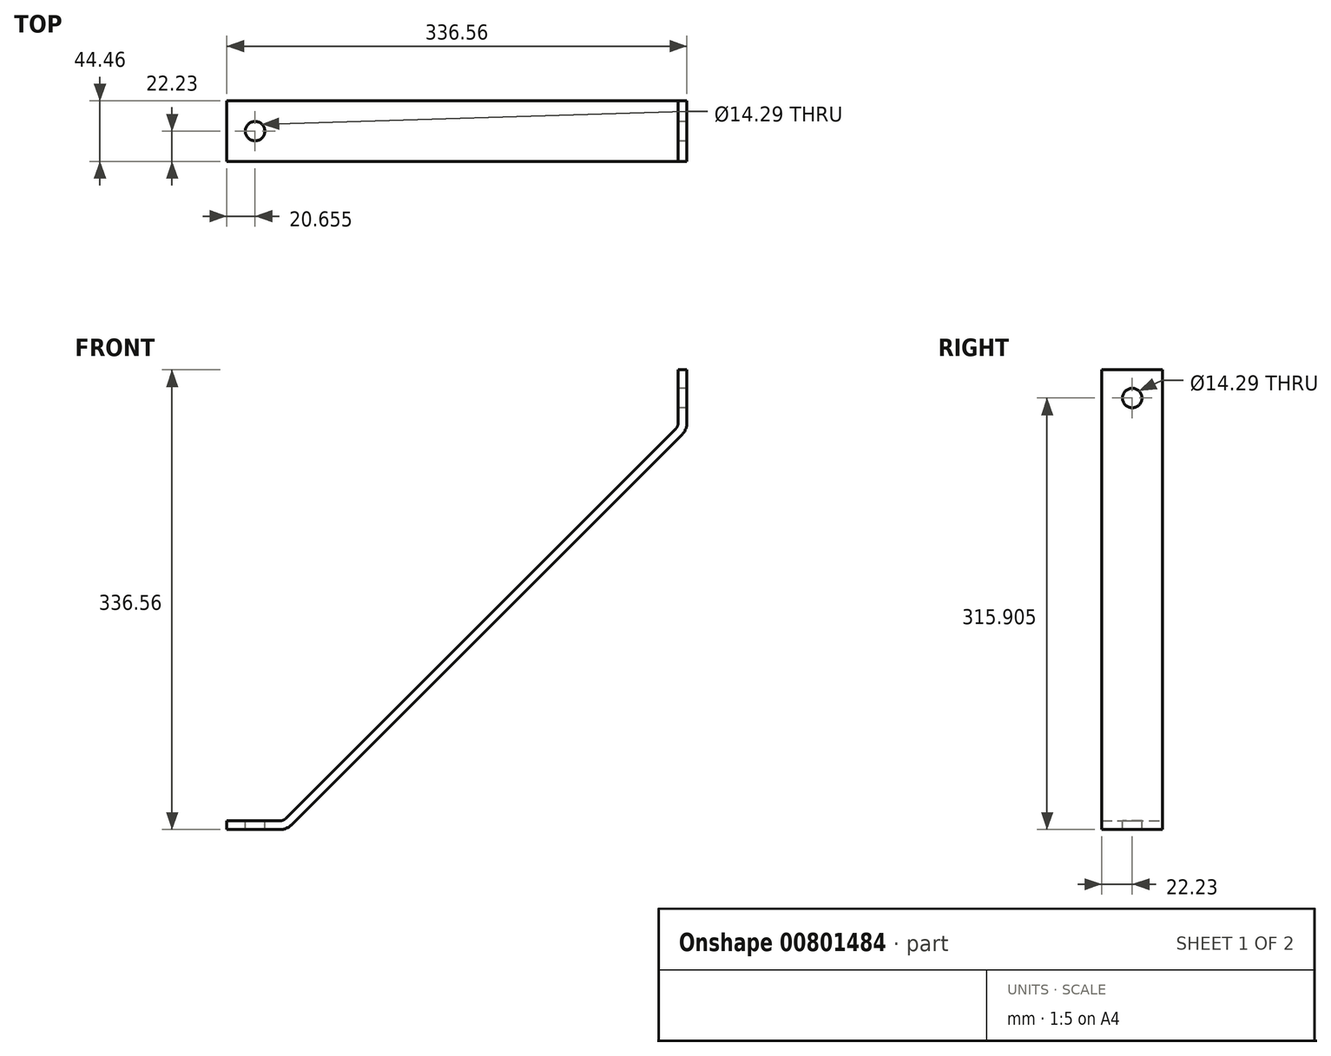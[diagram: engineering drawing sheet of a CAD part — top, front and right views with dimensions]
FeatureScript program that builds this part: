
annotation { "Feature Type Name" : "Feature", "Feature Type Description" : "" }
export const myFeature = defineFeature(function(context is Context, id is Id, definition is map)
    precondition{}
    {
        {
            var Q0;
            Q0=qCreatedBy(makeId("Front.planeOp"),FACE);
            var sketch = newSketch(context, id + "F0", { "sketchPlane" : qUnion([Q0])});
            skLineSegment(sketch, "E0.bottom", {"start": v(-124.37, -168.28) * mm, "end": v(-168.27, -168.28) * mm});
            skLineSegment(sketch, "E0.top", {"start": v(168.27, 168.28) * mm, "end": v(-168.28, 168.27) * mm});
            skLineSegment(sketch, "E0.left", {"start": v(168.27, 124.37) * mm, "end": v(168.27, 168.28) * mm});
            skLineSegment(sketch, "E0.right", {"start": v(-168.27, -168.28) * mm, "end": v(-168.27, -161.93) * mm});
            skPoint(sketch, "E0.middle", {"position": v(0, 0) * mm});
            skLineSegment(sketch, "E1.0", {"start": v(-127, -161.93) * mm, "end": v(-168.27, -161.93) * mm});
            skLineSegment(sketch, "E2", {"start": v(-168.27, -161.93) * mm, "end": v(-127, -161.93) * mm});
            skLineSegment(sketch, "E3", {"start": v(161.92, 168.28) * mm, "end": v(161.92, 127) * mm});
            skLineSegment(sketch, "E4", {"start": v(161.93, 127) * mm, "end": v(-127, -161.93) * mm});
            skLineSegment(sketch, "E5.0", {"start": v(168, 124.1) * mm, "end": v(-124.1, -168) * mm});
            skLineSegment(sketch, "E6", {"start": v(168, 124.1) * mm, "end": v(168.27, 124.37) * mm});
            skLineSegment(sketch, "E7", {"start": v(-124.1, -168) * mm, "end": v(-124.37, -168.28) * mm});
            skPoint(sketch, "E8.orphan", {"position": v(168.28, -168.27) * mm});
            skSolve(sketch);
        }
        {
            var Q0;
            Q0 = qSketchRegion(id + "F0", true);
            extrude(context, id + "F1", {"entities" : qUnion([Q0]), "endBound" : BoundingType.SYMMETRIC, "depth" : 44.45 * mm, "offsetDistance" : 25.4 * mm});
        }
        {
            var Q0;
            Q0=makeQuery(id+"F1.opExtrude","SWEPT_EDGE",EDGE,{"disambiguationData":[OSD([sQuery(id+"F0.wireOp",EDGE,"E2"),sQuery(id+"F0.wireOp",EDGE,"E4")])]});
            var Q1;
            Q1=makeQuery(id+"F1.opExtrude","SWEPT_EDGE",EDGE,{"disambiguationData":[OSD([sQuery(id+"F0.wireOp",EDGE,"E3"),sQuery(id+"F0.wireOp",EDGE,"E4")])]});
            fillet(context, id + "F2", {"entities" : qUnion([Q0, Q1]), "radius" : 6.35 * mm, "tangentPropagation" : true, "allowEdgeOverflow" : false});
        }
        {
            var Q0;
            Q0=makeQuery(id+"F1.opExtrude","SWEPT_EDGE",EDGE,{"disambiguationData":[OSD([sQuery(id+"F0.wireOp",EDGE,"E0.bottom"),sQuery(id+"F0.wireOp",EDGE,"E7")])]});
            var Q1;
            Q1=makeQuery(id+"F1.opExtrude","SWEPT_EDGE",EDGE,{"disambiguationData":[OSD([sQuery(id+"F0.wireOp",EDGE,"E0.left"),sQuery(id+"F0.wireOp",EDGE,"E6")])]});
            fillet(context, id + "F3", {"entities" : qUnion([Q0, Q1]), "radius" : 12.7 * mm, "tangentPropagation" : true, "allowEdgeOverflow" : false});
        }
        {
            var Q0;
            Q0=makeQuery(id+"F1.opExtrude","SWEPT_FACE",FACE,{"disambiguationData":[OSD([sQuery(id+"F0.wireOp",EDGE,"E3")])]});
            var sketch = newSketch(context, id + "F4", { "sketchPlane" : qUnion([Q0])});
            skCircle(sketch, "E9", {"center": v(0, 147.62) * mm, "radius": 7.14 * mm});
            skSolve(sketch);
        }
        {
            var Q0;
            Q0 = qSketchRegion(id + "F4", true);
            extrude(context, id + "F5", {"entities" : qUnion([Q0]), "operationType" : NewBodyOperationType.REMOVE, "oppositeDirection" : true, "depth" : 25.4 * mm, "offsetDistance" : 25.4 * mm});
        }
        {
            var Q0;
            Q0=qCreatedBy(makeId("Top.planeOp"),FACE);
            var sketch = newSketch(context, id + "F6", { "sketchPlane" : qUnion([Q0])});
            skCircle(sketch, "E10", {"center": v(-147.62, 0) * mm, "radius": 7.14 * mm});
            skSolve(sketch);
        }
        {
            var Q0;
            Q0 = qSketchRegion(id + "F6", true);
            extrude(context, id + "F7", {"entities" : qUnion([Q0]), "operationType" : NewBodyOperationType.REMOVE, "oppositeDirection" : true, "depth" : 206.5 * mm, "offsetDistance" : 25.4 * mm});
        }
    });
